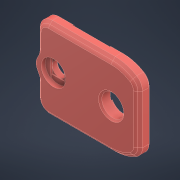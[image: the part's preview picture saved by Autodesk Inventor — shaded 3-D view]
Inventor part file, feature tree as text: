
AUTODESK INVENTOR PART (.ipt)
format: ipt  version: 2022.1 (Build 261234000, 234)  size: 543,232 bytes
history: native  units: mm
features: delete_face x8, chamfer x6, fillet x4, extrude x3, sketch x3, projected_geometry x3
ambient origin geometry x8: Origin, YZ Plane, XZ Plane, XY Plane, X Axis, Y Axis, Z Axis, Center Point
bodies: Volumenkörper2 (feature_tree), Volumenkörper1 (feature_tree)
feature tree (27):
  extrude  "Extrusion1"  Depth=18.0mm
  delete_face  "Fläche löschen2"
  delete_face  "Fläche löschen3"
  delete_face  "Fläche löschen4"
  delete_face  "Fläche löschen5"
  delete_face  "Fläche löschen6"
  delete_face  "Fläche löschen7"
  extrude  "Extrusion3"  TaperAngle=0.0deg  [1 undecoded]
  chamfer  "Fase2"  Distance=1.0mm Angle=45.0deg
  fillet  "Rundung6"  Radius=3.0mm
  chamfer  "Fase3"  Distance=1.0mm Angle=45.0deg
  fillet  "Rundung7"  Radius=3.0mm
  chamfer  "Fase4"  Distance=1.0mm Angle=45.0deg
  chamfer  "Fase5"  Distance=2.0mm Angle=45.0deg
  chamfer  "Fase6"  Distance=2.0mm Angle=45.0deg
  extrude  "Extrusion4"  Depth=1.0mm
  fillet  "Rundung8"  Radius=2.0mm
  delete_face  "Fläche löschen8"
  delete_face  "Fläche löschen9"
  chamfer  "Fase7"  Distance=2.0mm
  fillet  "Rundung9"  [1 undecoded]
  sketch  "Skizze1"  dims[d0=18.0mm d1=18.0mm]
  sketch  "Skizze3"  dims[d2=1.0mm d3=0.0mm d15=0.0mm d16=0.0mm d17=1.0mm d18=2.0mm d19=45.0deg d20=3.0mm d21=1.0mm d22=2.0mm d23=45.0deg d24=3.0mm d25=1.0mm d26=2.0mm d27=45.0deg d28=0.4mm d29=2.0mm d30=45.0deg d31=0.2mm d32=2.0mm d33=45.0deg]
  projected_geometry  "Projizierte Kontur3"
  projected_geometry  "Projizierte Kontur4"
  projected_geometry  "Projizierte Kontur5"
  sketch  "Skizze4"  dims[d34=2.0mm d35=0.0mm d36=1.0mm d37=0.2mm d38=2.0mm d39=45.0deg d40=2.0mm]
note: 2 required parameter values undecoded (feature->parameter linkage not recoverable at this tier; creation-order binding heuristic only, values carry confidence <= 0.55)
